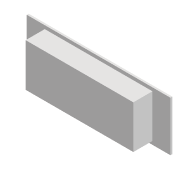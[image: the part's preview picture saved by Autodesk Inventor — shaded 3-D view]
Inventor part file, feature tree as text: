
AUTODESK INVENTOR PART (.ipt)
format: ipt  version: 2022 (Build 260153000, 153)  size: 90,624 bytes
history: native  units: mm
features: extrude x2, plane x2, sketch x2, projected_geometry x1
ambient origin geometry x8: Origin, YZ Plane, XZ Plane, XY Plane, X Axis, Y Axis, Z Axis, Center Point
bodies: Volumenkörper1 (feature_tree)
feature tree (7):
  extrude  "Extrusion1"  Depth=26.0mm
  extrude  "Extrusion2"  Depth=10.0mm TaperAngle=0.0deg
  plane  "Arbeitsebene1"
  plane  "Arbeitsebene2"
  sketch  "Skizze1"  dims[d0=75.0mm d1=26.0mm]
  sketch  "Skizze2"  dims[d2=1.0mm d3=0.0mm d4=10.0mm d5=0.0mm]
  projected_geometry  "Projizierte Kontur1"
